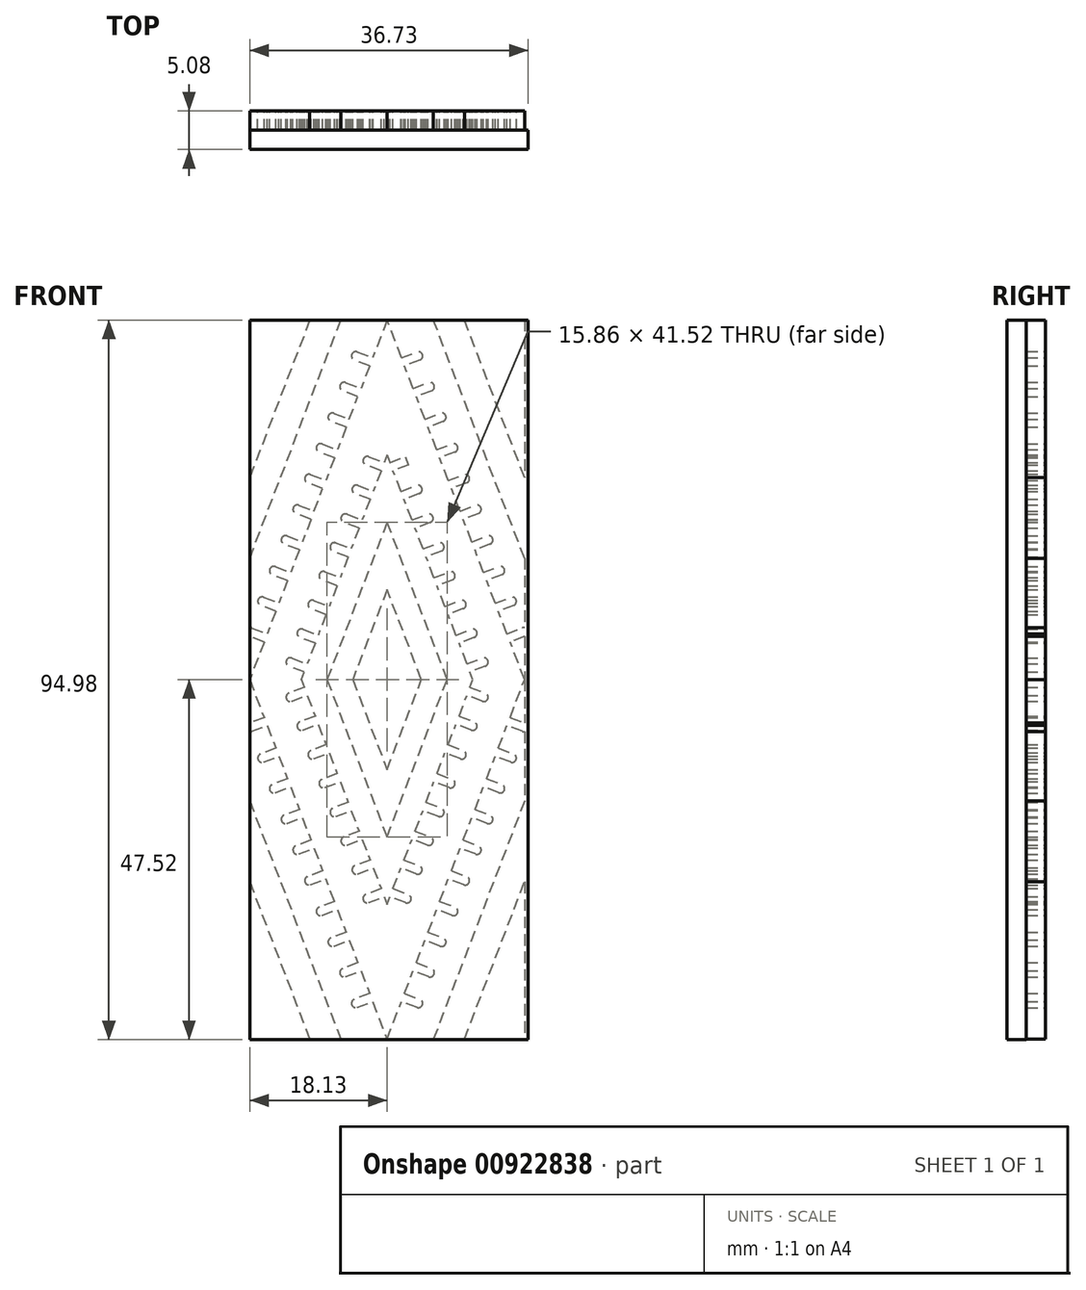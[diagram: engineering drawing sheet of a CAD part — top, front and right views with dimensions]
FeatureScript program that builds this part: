
annotation { "Feature Type Name" : "Feature", "Feature Type Description" : "" }
export const myFeature = defineFeature(function(context is Context, id is Id, definition is map)
    precondition{}
    {
        {
            var Q0;
            Q0=qCreatedBy(makeId("Front.planeOp"),FACE);
            var sketch = newSketch(context, id + "F0", { "sketchPlane" : qUnion([Q0])});
            skLineSegment(sketch, "E0.bottom", {"start": v(-18.13, 47.46) * mm, "end": v(18.13, 47.46) * mm});
            skLineSegment(sketch, "E0.top", {"start": v(-18.13, -47.46) * mm, "end": v(18.13, -47.46) * mm});
            skLineSegment(sketch, "E0.left", {"start": v(-18.13, 47.46) * mm, "end": v(-18.13, -47.46) * mm});
            skLineSegment(sketch, "E0.right", {"start": v(18.13, 47.46) * mm, "end": v(18.13, -47.46) * mm});
            skPoint(sketch, "E0.middle", {"position": v(0, 0) * mm});
            skLineSegment(sketch, "E1", {"start": v(0, 47.46) * mm, "end": v(-1.9, 42.47) * mm});
            skLineSegment(sketch, "E2", {"start": v(-18.13, 0) * mm, "end": v(-16.22, -4.98) * mm});
            skLineSegment(sketch, "E3", {"start": v(0, -47.46) * mm, "end": v(1.9, -42.47) * mm});
            skLineSegment(sketch, "E4", {"start": v(18.13, 0) * mm, "end": v(16.22, 4.98) * mm});
            skLineSegment(sketch, "E5.0", {"start": v(-3.4, 47.46) * mm, "end": v(-18.13, 8.9) * mm});
            skLineSegment(sketch, "E5.1", {"start": v(18.13, 8.9) * mm, "end": v(3.4, 47.46) * mm});
            skLineSegment(sketch, "E5.2", {"start": v(3.4, -47.46) * mm, "end": v(18.13, -8.9) * mm});
            skLineSegment(sketch, "E5.3", {"start": v(-18.13, -8.9) * mm, "end": v(-3.4, -47.46) * mm});
            skLineSegment(sketch, "E6.0", {"start": v(-10.2, 47.46) * mm, "end": v(-18.13, 26.7) * mm});
            skLineSegment(sketch, "E7.0", {"start": v(18.13, 26.7) * mm, "end": v(10.2, 47.46) * mm});
            skLineSegment(sketch, "E8.0", {"start": v(0, 29.66) * mm, "end": v(-0.39, 28.65) * mm});
            skLineSegment(sketch, "E8.1", {"start": v(11.33, 0) * mm, "end": v(10.94, 1) * mm});
            skLineSegment(sketch, "E8.2", {"start": v(0, -29.66) * mm, "end": v(0.39, -28.65) * mm});
            skLineSegment(sketch, "E8.3", {"start": v(-11.33, 0) * mm, "end": v(-10.94, -1) * mm});
            skLineSegment(sketch, "E9.0", {"start": v(4.53, 0) * mm, "end": v(0, 11.86) * mm});
            skLineSegment(sketch, "E9.1", {"start": v(0, -11.86) * mm, "end": v(4.53, 0) * mm});
            skLineSegment(sketch, "E9.2", {"start": v(-4.53, 0) * mm, "end": v(0, -11.86) * mm});
            skLineSegment(sketch, "E9.3", {"start": v(0, 11.86) * mm, "end": v(-4.53, 0) * mm});
            skLineSegment(sketch, "E10.0", {"start": v(0, 20.76) * mm, "end": v(-7.93, 0) * mm});
            skLineSegment(sketch, "E10.1", {"start": v(7.93, 0) * mm, "end": v(0, 20.76) * mm});
            skLineSegment(sketch, "E10.2", {"start": v(0, -20.76) * mm, "end": v(7.93, 0) * mm});
            skLineSegment(sketch, "E10.3", {"start": v(-7.93, 0) * mm, "end": v(0, -20.76) * mm});
            skLineSegment(sketch, "E11", {"start": v(-10.94, 1) * mm, "end": v(-12.96, 1.78) * mm});
            skLineSegment(sketch, "E12", {"start": v(-12.96, 1.78) * mm, "end": v(-12.55, 2.85) * mm});
            skLineSegment(sketch, "E13", {"start": v(-12.55, 2.85) * mm, "end": v(-10.54, 2.08) * mm});
            skArc(sketch, "E14", {"start": v(-12.55, 2.85) * mm, "mid": v(-13.3, 2.52) * mm, "end": v(-12.96, 1.78) * mm});
            skLineSegment(sketch, "E15.1.0.0", {"start": v(-9.5, 4.8) * mm, "end": v(-11.51, 5.58) * mm});
            skLineSegment(sketch, "E15.1.0.1", {"start": v(-11.1, 6.64) * mm, "end": v(-9.09, 5.87) * mm});
            skArc(sketch, "E15.1.0.2", {"start": v(-11.1, 6.64) * mm, "mid": v(-11.84, 6.31) * mm, "end": v(-11.51, 5.58) * mm});
            skLineSegment(sketch, "E15.2.0.0", {"start": v(-8.04, 8.6) * mm, "end": v(-10.06, 9.37) * mm});
            skLineSegment(sketch, "E15.2.0.1", {"start": v(-9.65, 10.44) * mm, "end": v(-7.64, 9.67) * mm});
            skArc(sketch, "E15.2.0.2", {"start": v(-9.65, 10.44) * mm, "mid": v(-10.4, 10.1) * mm, "end": v(-10.06, 9.37) * mm});
            skLineSegment(sketch, "E15.direction1", {"start": v(-12.96, 1.78) * mm, "end": v(-11.51, 5.58) * mm, "construction": true});
            skLineSegment(sketch, "E16.0.3.0", {"start": v(-6.6, 12.4) * mm, "end": v(-8.61, 13.17) * mm});
            skLineSegment(sketch, "E16.3.3.0", {"start": v(-8.2, 14.24) * mm, "end": v(-6.19, 13.47) * mm});
            skArc(sketch, "E16.6.3.0", {"start": v(-8.2, 14.24) * mm, "mid": v(-8.94, 13.9) * mm, "end": v(-8.61, 13.17) * mm});
            skLineSegment(sketch, "E16.0.4.0", {"start": v(-5.14, 16.2) * mm, "end": v(-7.16, 16.96) * mm});
            skLineSegment(sketch, "E16.3.4.0", {"start": v(-6.75, 18.03) * mm, "end": v(-4.74, 17.26) * mm});
            skArc(sketch, "E16.6.4.0", {"start": v(-6.75, 18.03) * mm, "mid": v(-7.5, 17.7) * mm, "end": v(-7.16, 16.96) * mm});
            skLineSegment(sketch, "E16.0.5.0", {"start": v(-3.7, 20) * mm, "end": v(-5.71, 20.76) * mm});
            skLineSegment(sketch, "E16.3.5.0", {"start": v(-5.3, 21.83) * mm, "end": v(-3.29, 21.06) * mm});
            skArc(sketch, "E16.6.5.0", {"start": v(-5.3, 21.83) * mm, "mid": v(-6.04, 21.5) * mm, "end": v(-5.71, 20.76) * mm});
            skLineSegment(sketch, "E16.0.6.0", {"start": v(-2.24, 23.79) * mm, "end": v(-4.26, 24.56) * mm});
            skLineSegment(sketch, "E16.3.6.0", {"start": v(-3.85, 25.63) * mm, "end": v(-1.84, 24.86) * mm});
            skArc(sketch, "E16.6.6.0", {"start": v(-3.85, 25.63) * mm, "mid": v(-4.59, 25.3) * mm, "end": v(-4.26, 24.56) * mm});
            skLineSegment(sketch, "E17", {"start": v(-11.33, 0) * mm, "end": v(-10.94, 1) * mm});
            skLineSegment(sketch, "E18.0.7.0", {"start": v(-0.8, 27.58) * mm, "end": v(-2.8, 28.35) * mm});
            skLineSegment(sketch, "E18.3.7.0", {"start": v(-2.4, 29.42) * mm, "end": v(-0.39, 28.65) * mm});
            skArc(sketch, "E18.6.7.0", {"start": v(-2.4, 29.42) * mm, "mid": v(-3.14, 29.1) * mm, "end": v(-2.8, 28.35) * mm});
            skLineSegment(sketch, "E19", {"start": v(-10.94, -1) * mm, "end": v(-12.96, -1.78) * mm});
            skLineSegment(sketch, "E20", {"start": v(-12.96, -1.78) * mm, "end": v(-12.55, -2.85) * mm});
            skLineSegment(sketch, "E21", {"start": v(-12.55, -2.85) * mm, "end": v(-10.54, -2.08) * mm});
            skArc(sketch, "E22", {"start": v(-12.96, -1.78) * mm, "mid": v(-13.3, -2.52) * mm, "end": v(-12.55, -2.85) * mm});
            skLineSegment(sketch, "E23.1.0.0", {"start": v(-11.1, -6.64) * mm, "end": v(-9.09, -5.87) * mm});
            skLineSegment(sketch, "E23.1.0.1", {"start": v(-9.5, -4.8) * mm, "end": v(-11.51, -5.58) * mm});
            skArc(sketch, "E23.1.0.2", {"start": v(-11.51, -5.58) * mm, "mid": v(-11.84, -6.31) * mm, "end": v(-11.1, -6.64) * mm});
            skLineSegment(sketch, "E23.2.0.0", {"start": v(-9.65, -10.44) * mm, "end": v(-7.64, -9.67) * mm});
            skLineSegment(sketch, "E23.2.0.1", {"start": v(-8.04, -8.6) * mm, "end": v(-10.06, -9.37) * mm});
            skArc(sketch, "E23.2.0.2", {"start": v(-10.06, -9.37) * mm, "mid": v(-10.4, -10.1) * mm, "end": v(-9.65, -10.44) * mm});
            skLineSegment(sketch, "E23.direction1", {"start": v(-12.55, -2.85) * mm, "end": v(-11.1, -6.64) * mm, "construction": true});
            skLineSegment(sketch, "E24.0.3.0", {"start": v(-8.2, -14.24) * mm, "end": v(-6.19, -13.47) * mm});
            skLineSegment(sketch, "E24.3.3.0", {"start": v(-6.6, -12.4) * mm, "end": v(-8.61, -13.17) * mm});
            skArc(sketch, "E24.6.3.0", {"start": v(-8.61, -13.17) * mm, "mid": v(-8.94, -13.9) * mm, "end": v(-8.2, -14.24) * mm});
            skLineSegment(sketch, "E24.0.4.0", {"start": v(-6.75, -18.03) * mm, "end": v(-4.74, -17.26) * mm});
            skLineSegment(sketch, "E24.3.4.0", {"start": v(-5.14, -16.2) * mm, "end": v(-7.16, -16.96) * mm});
            skArc(sketch, "E24.6.4.0", {"start": v(-7.16, -16.96) * mm, "mid": v(-7.5, -17.7) * mm, "end": v(-6.75, -18.03) * mm});
            skLineSegment(sketch, "E24.0.5.0", {"start": v(-5.3, -21.83) * mm, "end": v(-3.29, -21.06) * mm});
            skLineSegment(sketch, "E24.3.5.0", {"start": v(-3.7, -20) * mm, "end": v(-5.71, -20.76) * mm});
            skArc(sketch, "E24.6.5.0", {"start": v(-5.71, -20.76) * mm, "mid": v(-6.04, -21.5) * mm, "end": v(-5.3, -21.83) * mm});
            skLineSegment(sketch, "E24.0.6.0", {"start": v(-3.85, -25.63) * mm, "end": v(-1.84, -24.86) * mm});
            skLineSegment(sketch, "E24.3.6.0", {"start": v(-2.24, -23.79) * mm, "end": v(-4.26, -24.56) * mm});
            skArc(sketch, "E24.6.6.0", {"start": v(-4.26, -24.56) * mm, "mid": v(-4.59, -25.3) * mm, "end": v(-3.85, -25.63) * mm});
            skLineSegment(sketch, "E24.0.7.0", {"start": v(-2.4, -29.42) * mm, "end": v(-0.39, -28.65) * mm});
            skLineSegment(sketch, "E24.3.7.0", {"start": v(-0.8, -27.58) * mm, "end": v(-2.8, -28.35) * mm});
            skArc(sketch, "E24.6.7.0", {"start": v(-2.8, -28.35) * mm, "mid": v(-3.14, -29.1) * mm, "end": v(-2.4, -29.42) * mm});
            skLineSegment(sketch, "E25", {"start": v(18.13, 47.46) * mm, "end": v(-18.13, -47.46) * mm, "construction": true});
            skLineSegment(sketch, "E26", {"start": v(-18.13, 47.46) * mm, "end": v(18.13, -47.46) * mm, "construction": true});
            skLineSegment(sketch, "E27", {"start": v(0, 47.46) * mm, "end": v(0, -47.46) * mm, "construction": true});
            skLineSegment(sketch, "E28", {"start": v(-18.13, 0) * mm, "end": v(18.13, 0) * mm, "construction": true});
            skLineSegment(sketch, "E29", {"start": v(0, 29.66) * mm, "end": v(0.39, 28.65) * mm});
            skLineSegment(sketch, "E30", {"start": v(0.39, 28.65) * mm, "end": v(2.4, 29.42) * mm});
            skLineSegment(sketch, "E31", {"start": v(2.4, 29.42) * mm, "end": v(2.8, 28.35) * mm});
            skLineSegment(sketch, "E32", {"start": v(2.8, 28.35) * mm, "end": v(0.8, 27.58) * mm});
            skArc(sketch, "E33", {"start": v(2.8, 28.35) * mm, "mid": v(3.14, 29.1) * mm, "end": v(2.4, 29.42) * mm});
            skLineSegment(sketch, "E34.1.0.0", {"start": v(1.84, 24.86) * mm, "end": v(3.85, 25.63) * mm});
            skArc(sketch, "E34.1.0.1", {"start": v(4.26, 24.56) * mm, "mid": v(4.59, 25.3) * mm, "end": v(3.85, 25.63) * mm});
            skLineSegment(sketch, "E34.1.0.2", {"start": v(4.26, 24.56) * mm, "end": v(2.24, 23.79) * mm});
            skLineSegment(sketch, "E34.2.0.0", {"start": v(3.29, 21.06) * mm, "end": v(5.3, 21.83) * mm});
            skArc(sketch, "E34.2.0.1", {"start": v(5.71, 20.76) * mm, "mid": v(6.04, 21.5) * mm, "end": v(5.3, 21.83) * mm});
            skLineSegment(sketch, "E34.2.0.2", {"start": v(5.71, 20.76) * mm, "end": v(3.7, 20) * mm});
            skLineSegment(sketch, "E34.direction1", {"start": v(0.8, 27.58) * mm, "end": v(1.84, 24.86) * mm, "construction": true});
            skLineSegment(sketch, "E35.0.3.0", {"start": v(4.74, 17.26) * mm, "end": v(6.75, 18.03) * mm});
            skArc(sketch, "E35.3.3.0", {"start": v(7.16, 16.96) * mm, "mid": v(7.5, 17.7) * mm, "end": v(6.75, 18.03) * mm});
            skLineSegment(sketch, "E35.7.3.0", {"start": v(7.16, 16.96) * mm, "end": v(5.14, 16.2) * mm});
            skLineSegment(sketch, "E35.0.4.0", {"start": v(6.19, 13.47) * mm, "end": v(8.2, 14.24) * mm});
            skArc(sketch, "E35.3.4.0", {"start": v(8.61, 13.17) * mm, "mid": v(8.94, 13.9) * mm, "end": v(8.2, 14.24) * mm});
            skLineSegment(sketch, "E35.7.4.0", {"start": v(8.61, 13.17) * mm, "end": v(6.6, 12.4) * mm});
            skLineSegment(sketch, "E35.0.5.0", {"start": v(7.64, 9.67) * mm, "end": v(9.65, 10.44) * mm});
            skArc(sketch, "E35.3.5.0", {"start": v(10.06, 9.37) * mm, "mid": v(10.4, 10.1) * mm, "end": v(9.65, 10.44) * mm});
            skLineSegment(sketch, "E35.7.5.0", {"start": v(10.06, 9.37) * mm, "end": v(8.04, 8.6) * mm});
            skLineSegment(sketch, "E35.0.6.0", {"start": v(9.09, 5.87) * mm, "end": v(11.1, 6.64) * mm});
            skArc(sketch, "E35.3.6.0", {"start": v(11.51, 5.58) * mm, "mid": v(11.84, 6.31) * mm, "end": v(11.1, 6.64) * mm});
            skLineSegment(sketch, "E35.7.6.0", {"start": v(11.51, 5.58) * mm, "end": v(9.5, 4.8) * mm});
            skLineSegment(sketch, "E35.0.7.0", {"start": v(10.54, 2.08) * mm, "end": v(12.55, 2.85) * mm});
            skArc(sketch, "E35.3.7.0", {"start": v(12.96, 1.78) * mm, "mid": v(13.3, 2.52) * mm, "end": v(12.55, 2.85) * mm});
            skLineSegment(sketch, "E35.7.7.0", {"start": v(12.96, 1.78) * mm, "end": v(10.94, 1) * mm});
            skLineSegment(sketch, "E36", {"start": v(10.94, -1) * mm, "end": v(12.96, -1.78) * mm});
            skLineSegment(sketch, "E37", {"start": v(12.96, -1.78) * mm, "end": v(12.55, -2.85) * mm});
            skLineSegment(sketch, "E38", {"start": v(12.55, -2.85) * mm, "end": v(10.54, -2.08) * mm});
            skArc(sketch, "E39", {"start": v(12.55, -2.85) * mm, "mid": v(13.3, -2.52) * mm, "end": v(12.96, -1.78) * mm});
            skLineSegment(sketch, "E40", {"start": v(-16.22, 4.98) * mm, "end": v(-18.24, 5.75) * mm});
            skLineSegment(sketch, "E41", {"start": v(-18.24, 5.75) * mm, "end": v(-17.83, 6.82) * mm});
            skLineSegment(sketch, "E42", {"start": v(-17.83, 6.82) * mm, "end": v(-15.82, 6.05) * mm});
            skArc(sketch, "E43", {"start": v(-17.83, 6.82) * mm, "mid": v(-18.57, 6.5) * mm, "end": v(-18.24, 5.75) * mm});
            skLineSegment(sketch, "E44.1.0.0", {"start": v(11.1, -6.64) * mm, "end": v(9.09, -5.87) * mm});
            skLineSegment(sketch, "E44.1.0.1", {"start": v(9.5, -4.8) * mm, "end": v(11.51, -5.58) * mm});
            skArc(sketch, "E44.1.0.2", {"start": v(11.1, -6.64) * mm, "mid": v(11.84, -6.31) * mm, "end": v(11.51, -5.58) * mm});
            skLineSegment(sketch, "E44.2.0.0", {"start": v(9.65, -10.44) * mm, "end": v(7.64, -9.67) * mm});
            skLineSegment(sketch, "E44.2.0.1", {"start": v(8.04, -8.6) * mm, "end": v(10.06, -9.37) * mm});
            skArc(sketch, "E44.2.0.2", {"start": v(9.65, -10.44) * mm, "mid": v(10.4, -10.1) * mm, "end": v(10.06, -9.37) * mm});
            skLineSegment(sketch, "E44.3.0.0", {"start": v(8.2, -14.24) * mm, "end": v(6.19, -13.47) * mm});
            skLineSegment(sketch, "E44.3.0.1", {"start": v(6.6, -12.4) * mm, "end": v(8.61, -13.17) * mm});
            skArc(sketch, "E44.3.0.2", {"start": v(8.2, -14.24) * mm, "mid": v(8.94, -13.9) * mm, "end": v(8.61, -13.17) * mm});
            skLineSegment(sketch, "E44.4.0.0", {"start": v(6.75, -18.03) * mm, "end": v(4.74, -17.26) * mm});
            skLineSegment(sketch, "E44.4.0.1", {"start": v(5.14, -16.2) * mm, "end": v(7.16, -16.96) * mm});
            skArc(sketch, "E44.4.0.2", {"start": v(6.75, -18.03) * mm, "mid": v(7.5, -17.7) * mm, "end": v(7.16, -16.96) * mm});
            skLineSegment(sketch, "E44.5.0.0", {"start": v(5.3, -21.83) * mm, "end": v(3.29, -21.06) * mm});
            skLineSegment(sketch, "E44.5.0.1", {"start": v(3.7, -20) * mm, "end": v(5.71, -20.76) * mm});
            skArc(sketch, "E44.5.0.2", {"start": v(5.3, -21.83) * mm, "mid": v(6.04, -21.5) * mm, "end": v(5.71, -20.76) * mm});
            skLineSegment(sketch, "E44.6.0.0", {"start": v(3.85, -25.63) * mm, "end": v(1.84, -24.86) * mm});
            skLineSegment(sketch, "E44.6.0.1", {"start": v(2.24, -23.79) * mm, "end": v(4.26, -24.56) * mm});
            skArc(sketch, "E44.6.0.2", {"start": v(3.85, -25.63) * mm, "mid": v(4.59, -25.3) * mm, "end": v(4.26, -24.56) * mm});
            skLineSegment(sketch, "E44.7.0.0", {"start": v(2.4, -29.42) * mm, "end": v(0.39, -28.65) * mm});
            skLineSegment(sketch, "E44.7.0.1", {"start": v(0.8, -27.58) * mm, "end": v(2.8, -28.35) * mm});
            skArc(sketch, "E44.7.0.2", {"start": v(2.4, -29.42) * mm, "mid": v(3.14, -29.1) * mm, "end": v(2.8, -28.35) * mm});
            skLineSegment(sketch, "E44.direction1", {"start": v(10.54, -2.08) * mm, "end": v(9.5, -4.8) * mm, "construction": true});
            skLineSegment(sketch, "E45.1.0.0", {"start": v(-14.68, 9.03) * mm, "end": v(-16.7, 9.8) * mm});
            skLineSegment(sketch, "E45.1.0.1", {"start": v(-16.29, 10.87) * mm, "end": v(-14.27, 10.1) * mm});
            skArc(sketch, "E45.1.0.2", {"start": v(-16.29, 10.87) * mm, "mid": v(-17.02, 10.54) * mm, "end": v(-16.7, 9.8) * mm});
            skLineSegment(sketch, "E45.2.0.0", {"start": v(-13.13, 13.08) * mm, "end": v(-15.15, 13.85) * mm});
            skLineSegment(sketch, "E45.2.0.1", {"start": v(-14.74, 14.91) * mm, "end": v(-12.72, 14.14) * mm});
            skArc(sketch, "E45.2.0.2", {"start": v(-14.74, 14.91) * mm, "mid": v(-15.48, 14.58) * mm, "end": v(-15.15, 13.85) * mm});
            skLineSegment(sketch, "E45.3.0.0", {"start": v(-11.59, 17.12) * mm, "end": v(-13.6, 17.9) * mm});
            skLineSegment(sketch, "E45.3.0.1", {"start": v(-13.2, 18.96) * mm, "end": v(-11.18, 18.2) * mm});
            skArc(sketch, "E45.3.0.2", {"start": v(-13.2, 18.96) * mm, "mid": v(-13.93, 18.63) * mm, "end": v(-13.6, 17.9) * mm});
            skLineSegment(sketch, "E45.4.0.0", {"start": v(-10.04, 21.17) * mm, "end": v(-12.06, 21.94) * mm});
            skLineSegment(sketch, "E45.4.0.1", {"start": v(-11.65, 23) * mm, "end": v(-9.63, 22.24) * mm});
            skArc(sketch, "E45.4.0.2", {"start": v(-11.65, 23) * mm, "mid": v(-12.39, 22.68) * mm, "end": v(-12.06, 21.94) * mm});
            skLineSegment(sketch, "E45.5.0.0", {"start": v(-8.5, 25.22) * mm, "end": v(-10.51, 25.99) * mm});
            skLineSegment(sketch, "E45.5.0.1", {"start": v(-10.1, 27.06) * mm, "end": v(-8.09, 26.29) * mm});
            skArc(sketch, "E45.5.0.2", {"start": v(-10.1, 27.06) * mm, "mid": v(-10.84, 26.73) * mm, "end": v(-10.51, 25.99) * mm});
            skLineSegment(sketch, "E45.6.0.0", {"start": v(-6.95, 29.26) * mm, "end": v(-8.97, 30.03) * mm});
            skLineSegment(sketch, "E45.6.0.1", {"start": v(-8.56, 31.1) * mm, "end": v(-6.54, 30.33) * mm});
            skArc(sketch, "E45.6.0.2", {"start": v(-8.56, 31.1) * mm, "mid": v(-9.3, 30.77) * mm, "end": v(-8.97, 30.03) * mm});
            skLineSegment(sketch, "E45.7.0.0", {"start": v(-5.4, 33.31) * mm, "end": v(-7.42, 34.08) * mm});
            skLineSegment(sketch, "E45.7.0.1", {"start": v(-7.01, 35.15) * mm, "end": v(-5, 34.38) * mm});
            skArc(sketch, "E45.7.0.2", {"start": v(-7.01, 35.15) * mm, "mid": v(-7.75, 34.82) * mm, "end": v(-7.42, 34.08) * mm});
            skLineSegment(sketch, "E45.8.0.0", {"start": v(-3.86, 37.36) * mm, "end": v(-5.87, 38.13) * mm});
            skLineSegment(sketch, "E45.8.0.1", {"start": v(-5.47, 39.2) * mm, "end": v(-3.45, 38.43) * mm});
            skArc(sketch, "E45.8.0.2", {"start": v(-5.47, 39.2) * mm, "mid": v(-6.2, 38.87) * mm, "end": v(-5.87, 38.13) * mm});
            skLineSegment(sketch, "E45.9.0.0", {"start": v(-2.31, 41.4) * mm, "end": v(-4.33, 42.18) * mm});
            skLineSegment(sketch, "E45.9.0.1", {"start": v(-3.92, 43.24) * mm, "end": v(-1.9, 42.47) * mm});
            skArc(sketch, "E45.9.0.2", {"start": v(-3.92, 43.24) * mm, "mid": v(-4.66, 42.91) * mm, "end": v(-4.33, 42.18) * mm});
            skLineSegment(sketch, "E45.direction1", {"start": v(-18.24, 5.75) * mm, "end": v(-16.7, 9.8) * mm, "construction": true});
            skLineSegment(sketch, "E46", {"start": v(1.9, 42.47) * mm, "end": v(3.92, 43.24) * mm});
            skLineSegment(sketch, "E47", {"start": v(3.92, 43.24) * mm, "end": v(4.12, 42.7) * mm});
            skLineSegment(sketch, "E48", {"start": v(4.33, 42.18) * mm, "end": v(2.31, 41.4) * mm});
            skArc(sketch, "E49", {"start": v(4.33, 42.18) * mm, "mid": v(4.66, 42.91) * mm, "end": v(3.92, 43.24) * mm});
            skLineSegment(sketch, "E50.1.0.0", {"start": v(5.87, 38.13) * mm, "end": v(3.86, 37.36) * mm});
            skLineSegment(sketch, "E50.1.0.1", {"start": v(3.45, 38.43) * mm, "end": v(5.47, 39.2) * mm});
            skArc(sketch, "E50.1.0.2", {"start": v(5.87, 38.13) * mm, "mid": v(6.2, 38.87) * mm, "end": v(5.47, 39.2) * mm});
            skLineSegment(sketch, "E50.2.0.0", {"start": v(7.42, 34.08) * mm, "end": v(5.4, 33.31) * mm});
            skLineSegment(sketch, "E50.2.0.1", {"start": v(5, 34.38) * mm, "end": v(7.01, 35.15) * mm});
            skArc(sketch, "E50.2.0.2", {"start": v(7.42, 34.08) * mm, "mid": v(7.75, 34.82) * mm, "end": v(7.01, 35.15) * mm});
            skLineSegment(sketch, "E50.3.0.0", {"start": v(8.97, 30.03) * mm, "end": v(6.95, 29.26) * mm});
            skLineSegment(sketch, "E50.3.0.1", {"start": v(6.54, 30.33) * mm, "end": v(8.56, 31.1) * mm});
            skArc(sketch, "E50.3.0.2", {"start": v(8.97, 30.03) * mm, "mid": v(9.3, 30.77) * mm, "end": v(8.56, 31.1) * mm});
            skLineSegment(sketch, "E50.4.0.0", {"start": v(10.51, 25.99) * mm, "end": v(8.5, 25.22) * mm});
            skLineSegment(sketch, "E50.4.0.1", {"start": v(8.09, 26.29) * mm, "end": v(10.1, 27.06) * mm});
            skArc(sketch, "E50.4.0.2", {"start": v(10.51, 25.99) * mm, "mid": v(10.84, 26.73) * mm, "end": v(10.1, 27.06) * mm});
            skLineSegment(sketch, "E50.5.0.0", {"start": v(12.06, 21.94) * mm, "end": v(10.04, 21.17) * mm});
            skLineSegment(sketch, "E50.5.0.1", {"start": v(9.63, 22.24) * mm, "end": v(11.65, 23) * mm});
            skArc(sketch, "E50.5.0.2", {"start": v(12.06, 21.94) * mm, "mid": v(12.39, 22.68) * mm, "end": v(11.65, 23) * mm});
            skLineSegment(sketch, "E50.6.0.0", {"start": v(13.6, 17.9) * mm, "end": v(11.59, 17.12) * mm});
            skLineSegment(sketch, "E50.6.0.1", {"start": v(11.18, 18.2) * mm, "end": v(13.2, 18.96) * mm});
            skArc(sketch, "E50.6.0.2", {"start": v(13.6, 17.9) * mm, "mid": v(13.93, 18.63) * mm, "end": v(13.2, 18.96) * mm});
            skLineSegment(sketch, "E50.7.0.0", {"start": v(15.15, 13.85) * mm, "end": v(13.13, 13.08) * mm});
            skLineSegment(sketch, "E50.7.0.1", {"start": v(12.72, 14.14) * mm, "end": v(14.74, 14.91) * mm});
            skArc(sketch, "E50.7.0.2", {"start": v(15.15, 13.85) * mm, "mid": v(15.48, 14.58) * mm, "end": v(14.74, 14.91) * mm});
            skLineSegment(sketch, "E50.8.0.0", {"start": v(16.7, 9.8) * mm, "end": v(14.68, 9.03) * mm});
            skLineSegment(sketch, "E50.8.0.1", {"start": v(14.27, 10.1) * mm, "end": v(16.29, 10.87) * mm});
            skArc(sketch, "E50.8.0.2", {"start": v(16.7, 9.8) * mm, "mid": v(17.02, 10.54) * mm, "end": v(16.29, 10.87) * mm});
            skLineSegment(sketch, "E50.9.0.0", {"start": v(18.24, 5.75) * mm, "end": v(16.22, 4.98) * mm});
            skLineSegment(sketch, "E50.9.0.1", {"start": v(15.82, 6.05) * mm, "end": v(17.83, 6.82) * mm});
            skArc(sketch, "E50.9.0.2", {"start": v(18.24, 5.75) * mm, "mid": v(18.57, 6.5) * mm, "end": v(17.83, 6.82) * mm});
            skLineSegment(sketch, "E50.direction1", {"start": v(2.31, 41.4) * mm, "end": v(3.45, 38.43) * mm, "construction": true});
            skLineSegment(sketch, "E51", {"start": v(-16.22, -4.98) * mm, "end": v(-18.24, -5.75) * mm});
            skLineSegment(sketch, "E52", {"start": v(-18.24, -5.75) * mm, "end": v(-17.83, -6.82) * mm});
            skLineSegment(sketch, "E53", {"start": v(-17.83, -6.82) * mm, "end": v(-15.82, -6.05) * mm});
            skArc(sketch, "E54", {"start": v(-18.24, -5.75) * mm, "mid": v(-18.57, -6.5) * mm, "end": v(-17.83, -6.82) * mm});
            skLineSegment(sketch, "E55.1.0.0", {"start": v(-14.68, -9.03) * mm, "end": v(-16.7, -9.8) * mm});
            skLineSegment(sketch, "E55.1.0.1", {"start": v(-16.29, -10.87) * mm, "end": v(-14.27, -10.1) * mm});
            skArc(sketch, "E55.1.0.2", {"start": v(-16.7, -9.8) * mm, "mid": v(-17.02, -10.54) * mm, "end": v(-16.29, -10.87) * mm});
            skLineSegment(sketch, "E55.2.0.0", {"start": v(-13.13, -13.08) * mm, "end": v(-15.15, -13.85) * mm});
            skLineSegment(sketch, "E55.2.0.1", {"start": v(-14.74, -14.91) * mm, "end": v(-12.72, -14.14) * mm});
            skArc(sketch, "E55.2.0.2", {"start": v(-15.15, -13.85) * mm, "mid": v(-15.48, -14.58) * mm, "end": v(-14.74, -14.91) * mm});
            skLineSegment(sketch, "E55.3.0.0", {"start": v(-11.59, -17.12) * mm, "end": v(-13.6, -17.9) * mm});
            skLineSegment(sketch, "E55.3.0.1", {"start": v(-13.2, -18.96) * mm, "end": v(-11.18, -18.2) * mm});
            skArc(sketch, "E55.3.0.2", {"start": v(-13.6, -17.9) * mm, "mid": v(-13.93, -18.63) * mm, "end": v(-13.2, -18.96) * mm});
            skLineSegment(sketch, "E55.4.0.0", {"start": v(-10.04, -21.17) * mm, "end": v(-12.06, -21.94) * mm});
            skLineSegment(sketch, "E55.4.0.1", {"start": v(-11.65, -23) * mm, "end": v(-9.63, -22.24) * mm});
            skArc(sketch, "E55.4.0.2", {"start": v(-12.06, -21.94) * mm, "mid": v(-12.39, -22.68) * mm, "end": v(-11.65, -23) * mm});
            skLineSegment(sketch, "E55.5.0.0", {"start": v(-8.5, -25.22) * mm, "end": v(-10.51, -25.99) * mm});
            skLineSegment(sketch, "E55.5.0.1", {"start": v(-10.1, -27.06) * mm, "end": v(-8.09, -26.29) * mm});
            skArc(sketch, "E55.5.0.2", {"start": v(-10.51, -25.99) * mm, "mid": v(-10.84, -26.73) * mm, "end": v(-10.1, -27.06) * mm});
            skLineSegment(sketch, "E55.6.0.0", {"start": v(-6.95, -29.26) * mm, "end": v(-8.97, -30.03) * mm});
            skLineSegment(sketch, "E55.6.0.1", {"start": v(-8.56, -31.1) * mm, "end": v(-6.54, -30.33) * mm});
            skArc(sketch, "E55.6.0.2", {"start": v(-8.97, -30.03) * mm, "mid": v(-9.3, -30.77) * mm, "end": v(-8.56, -31.1) * mm});
            skLineSegment(sketch, "E55.7.0.0", {"start": v(-5.4, -33.31) * mm, "end": v(-7.42, -34.08) * mm});
            skLineSegment(sketch, "E55.7.0.1", {"start": v(-7.01, -35.15) * mm, "end": v(-5, -34.38) * mm});
            skArc(sketch, "E55.7.0.2", {"start": v(-7.42, -34.08) * mm, "mid": v(-7.75, -34.82) * mm, "end": v(-7.01, -35.15) * mm});
            skLineSegment(sketch, "E55.8.0.0", {"start": v(-3.86, -37.36) * mm, "end": v(-5.87, -38.13) * mm});
            skLineSegment(sketch, "E55.8.0.1", {"start": v(-5.47, -39.2) * mm, "end": v(-3.45, -38.43) * mm});
            skArc(sketch, "E55.8.0.2", {"start": v(-5.87, -38.13) * mm, "mid": v(-6.2, -38.87) * mm, "end": v(-5.47, -39.2) * mm});
            skLineSegment(sketch, "E55.9.0.0", {"start": v(-2.31, -41.4) * mm, "end": v(-4.33, -42.18) * mm});
            skLineSegment(sketch, "E55.9.0.1", {"start": v(-3.92, -43.24) * mm, "end": v(-1.9, -42.47) * mm});
            skArc(sketch, "E55.9.0.2", {"start": v(-4.33, -42.18) * mm, "mid": v(-4.66, -42.91) * mm, "end": v(-3.92, -43.24) * mm});
            skLineSegment(sketch, "E55.direction1", {"start": v(-18.24, -5.75) * mm, "end": v(-16.7, -9.8) * mm, "construction": true});
            skLineSegment(sketch, "E56", {"start": v(16.22, -4.98) * mm, "end": v(18.24, -5.75) * mm});
            skLineSegment(sketch, "E57", {"start": v(18.24, -5.75) * mm, "end": v(17.83, -6.82) * mm});
            skLineSegment(sketch, "E58", {"start": v(17.83, -6.82) * mm, "end": v(15.82, -6.05) * mm});
            skArc(sketch, "E59", {"start": v(17.83, -6.82) * mm, "mid": v(18.57, -6.5) * mm, "end": v(18.24, -5.75) * mm});
            skLineSegment(sketch, "E60.1.0.0", {"start": v(14.68, -9.03) * mm, "end": v(16.7, -9.8) * mm});
            skLineSegment(sketch, "E60.1.0.1", {"start": v(16.29, -10.87) * mm, "end": v(14.27, -10.1) * mm});
            skArc(sketch, "E60.1.0.2", {"start": v(16.29, -10.87) * mm, "mid": v(17.02, -10.54) * mm, "end": v(16.7, -9.8) * mm});
            skLineSegment(sketch, "E60.2.0.0", {"start": v(13.13, -13.08) * mm, "end": v(15.15, -13.85) * mm});
            skLineSegment(sketch, "E60.2.0.1", {"start": v(14.74, -14.91) * mm, "end": v(12.72, -14.14) * mm});
            skArc(sketch, "E60.2.0.2", {"start": v(14.74, -14.91) * mm, "mid": v(15.48, -14.58) * mm, "end": v(15.15, -13.85) * mm});
            skLineSegment(sketch, "E60.3.0.0", {"start": v(11.59, -17.12) * mm, "end": v(13.6, -17.9) * mm});
            skLineSegment(sketch, "E60.3.0.1", {"start": v(13.2, -18.96) * mm, "end": v(11.18, -18.2) * mm});
            skArc(sketch, "E60.3.0.2", {"start": v(13.2, -18.96) * mm, "mid": v(13.93, -18.63) * mm, "end": v(13.6, -17.9) * mm});
            skLineSegment(sketch, "E60.4.0.0", {"start": v(10.04, -21.17) * mm, "end": v(12.06, -21.94) * mm});
            skLineSegment(sketch, "E60.4.0.1", {"start": v(11.65, -23) * mm, "end": v(9.63, -22.24) * mm});
            skArc(sketch, "E60.4.0.2", {"start": v(11.65, -23) * mm, "mid": v(12.39, -22.68) * mm, "end": v(12.06, -21.94) * mm});
            skLineSegment(sketch, "E60.5.0.0", {"start": v(8.5, -25.22) * mm, "end": v(10.51, -25.99) * mm});
            skLineSegment(sketch, "E60.5.0.1", {"start": v(10.1, -27.06) * mm, "end": v(8.09, -26.29) * mm});
            skArc(sketch, "E60.5.0.2", {"start": v(10.1, -27.06) * mm, "mid": v(10.84, -26.73) * mm, "end": v(10.51, -25.99) * mm});
            skLineSegment(sketch, "E60.6.0.0", {"start": v(6.95, -29.26) * mm, "end": v(8.97, -30.03) * mm});
            skLineSegment(sketch, "E60.6.0.1", {"start": v(8.56, -31.1) * mm, "end": v(6.54, -30.33) * mm});
            skArc(sketch, "E60.6.0.2", {"start": v(8.56, -31.1) * mm, "mid": v(9.3, -30.77) * mm, "end": v(8.97, -30.03) * mm});
            skLineSegment(sketch, "E60.7.0.0", {"start": v(5.4, -33.31) * mm, "end": v(7.42, -34.08) * mm});
            skLineSegment(sketch, "E60.7.0.1", {"start": v(7.01, -35.15) * mm, "end": v(5, -34.38) * mm});
            skArc(sketch, "E60.7.0.2", {"start": v(7.01, -35.15) * mm, "mid": v(7.75, -34.82) * mm, "end": v(7.42, -34.08) * mm});
            skLineSegment(sketch, "E60.8.0.0", {"start": v(3.86, -37.36) * mm, "end": v(5.87, -38.13) * mm});
            skLineSegment(sketch, "E60.8.0.1", {"start": v(5.47, -39.2) * mm, "end": v(3.45, -38.43) * mm});
            skArc(sketch, "E60.8.0.2", {"start": v(5.47, -39.2) * mm, "mid": v(6.2, -38.87) * mm, "end": v(5.87, -38.13) * mm});
            skLineSegment(sketch, "E60.9.0.0", {"start": v(2.31, -41.4) * mm, "end": v(4.33, -42.18) * mm});
            skLineSegment(sketch, "E60.9.0.1", {"start": v(3.92, -43.24) * mm, "end": v(1.9, -42.47) * mm});
            skArc(sketch, "E60.9.0.2", {"start": v(3.92, -43.24) * mm, "mid": v(4.66, -42.91) * mm, "end": v(4.33, -42.18) * mm});
            skLineSegment(sketch, "E60.direction1", {"start": v(15.82, -6.05) * mm, "end": v(14.68, -9.03) * mm, "construction": true});
            skLineSegment(sketch, "E61.0", {"start": v(-18.13, -26.7) * mm, "end": v(-10.2, -47.46) * mm});
            skLineSegment(sketch, "E62.0", {"start": v(10.2, -47.46) * mm, "end": v(18.13, -26.7) * mm});
            skLineSegment(sketch, "E63.trimOffspring", {"start": v(2.31, -41.4) * mm, "end": v(3.45, -38.43) * mm});
            skLineSegment(sketch, "E64.trimOffspring", {"start": v(3.86, -37.36) * mm, "end": v(5, -34.38) * mm});
            skLineSegment(sketch, "E65.trimOffspring", {"start": v(5.4, -33.31) * mm, "end": v(6.54, -30.33) * mm});
            skLineSegment(sketch, "E66.trimOffspring", {"start": v(6.95, -29.26) * mm, "end": v(8.09, -26.29) * mm});
            skLineSegment(sketch, "E67.trimOffspring", {"start": v(8.5, -25.22) * mm, "end": v(9.63, -22.24) * mm});
            skLineSegment(sketch, "E68.trimOffspring", {"start": v(10.04, -21.17) * mm, "end": v(11.18, -18.2) * mm});
            skLineSegment(sketch, "E69.trimOffspring", {"start": v(11.59, -17.12) * mm, "end": v(12.72, -14.14) * mm});
            skLineSegment(sketch, "E70.trimOffspring", {"start": v(13.13, -13.08) * mm, "end": v(14.27, -10.1) * mm});
            skLineSegment(sketch, "E71.trimOffspring", {"start": v(14.68, -9.03) * mm, "end": v(15.82, -6.05) * mm});
            skLineSegment(sketch, "E72.trimOffspring", {"start": v(16.22, -4.98) * mm, "end": v(18.13, 0) * mm});
            skLineSegment(sketch, "E73.trimOffspring", {"start": v(10.94, -1) * mm, "end": v(11.33, 0) * mm});
            skLineSegment(sketch, "E74.trimOffspring", {"start": v(9.5, -4.8) * mm, "end": v(10.54, -2.08) * mm});
            skLineSegment(sketch, "E75.trimOffspring", {"start": v(8.04, -8.6) * mm, "end": v(9.09, -5.87) * mm});
            skLineSegment(sketch, "E76.trimOffspring", {"start": v(6.6, -12.4) * mm, "end": v(7.64, -9.67) * mm});
            skLineSegment(sketch, "E77.trimOffspring", {"start": v(5.14, -16.2) * mm, "end": v(6.19, -13.47) * mm});
            skLineSegment(sketch, "E78.trimOffspring", {"start": v(3.7, -20) * mm, "end": v(4.74, -17.26) * mm});
            skLineSegment(sketch, "E79.trimOffspring", {"start": v(2.24, -23.79) * mm, "end": v(3.29, -21.06) * mm});
            skLineSegment(sketch, "E80.trimOffspring", {"start": v(0.8, -27.58) * mm, "end": v(1.84, -24.86) * mm});
            skLineSegment(sketch, "E81.trimOffspring", {"start": v(-0.39, -28.65) * mm, "end": v(0, -29.66) * mm});
            skLineSegment(sketch, "E82.trimOffspring", {"start": v(-1.84, -24.86) * mm, "end": v(-0.8, -27.58) * mm});
            skLineSegment(sketch, "E83.trimOffspring", {"start": v(-3.29, -21.06) * mm, "end": v(-2.24, -23.79) * mm});
            skLineSegment(sketch, "E84.trimOffspring", {"start": v(-4.74, -17.26) * mm, "end": v(-3.7, -20) * mm});
            skLineSegment(sketch, "E85.trimOffspring", {"start": v(-6.19, -13.47) * mm, "end": v(-5.14, -16.2) * mm});
            skLineSegment(sketch, "E86.trimOffspring", {"start": v(-7.64, -9.67) * mm, "end": v(-6.6, -12.4) * mm});
            skLineSegment(sketch, "E87.trimOffspring", {"start": v(-9.09, -5.87) * mm, "end": v(-8.04, -8.6) * mm});
            skLineSegment(sketch, "E88.trimOffspring", {"start": v(-10.54, -2.08) * mm, "end": v(-9.5, -4.8) * mm});
            skLineSegment(sketch, "E89.trimOffspring", {"start": v(-10.94, 1) * mm, "end": v(-11.33, 0) * mm});
            skLineSegment(sketch, "E90.trimOffspring", {"start": v(-9.5, 4.8) * mm, "end": v(-10.54, 2.08) * mm});
            skLineSegment(sketch, "E91.trimOffspring", {"start": v(-8.04, 8.6) * mm, "end": v(-9.09, 5.87) * mm});
            skLineSegment(sketch, "E92.trimOffspring", {"start": v(-6.6, 12.4) * mm, "end": v(-7.64, 9.67) * mm});
            skLineSegment(sketch, "E93.trimOffspring", {"start": v(-5.14, 16.2) * mm, "end": v(-6.19, 13.47) * mm});
            skLineSegment(sketch, "E94.trimOffspring", {"start": v(-3.7, 20) * mm, "end": v(-4.74, 17.26) * mm});
            skLineSegment(sketch, "E95.trimOffspring", {"start": v(-2.24, 23.79) * mm, "end": v(-3.29, 21.06) * mm});
            skLineSegment(sketch, "E96.trimOffspring", {"start": v(-0.8, 27.58) * mm, "end": v(-1.84, 24.86) * mm});
            skLineSegment(sketch, "E97.trimOffspring", {"start": v(0.39, 28.65) * mm, "end": v(0, 29.66) * mm});
            skLineSegment(sketch, "E98.trimOffspring", {"start": v(1.84, 24.86) * mm, "end": v(0.8, 27.58) * mm});
            skLineSegment(sketch, "E99.trimOffspring", {"start": v(3.29, 21.06) * mm, "end": v(2.24, 23.79) * mm});
            skLineSegment(sketch, "E100.trimOffspring", {"start": v(4.74, 17.26) * mm, "end": v(3.7, 20) * mm});
            skLineSegment(sketch, "E101.trimOffspring", {"start": v(6.19, 13.47) * mm, "end": v(5.14, 16.2) * mm});
            skLineSegment(sketch, "E102.trimOffspring", {"start": v(7.64, 9.67) * mm, "end": v(6.6, 12.4) * mm});
            skLineSegment(sketch, "E103.trimOffspring", {"start": v(9.09, 5.87) * mm, "end": v(8.04, 8.6) * mm});
            skLineSegment(sketch, "E104.trimOffspring", {"start": v(10.54, 2.08) * mm, "end": v(9.5, 4.8) * mm});
            skLineSegment(sketch, "E105.trimOffspring", {"start": v(15.82, 6.05) * mm, "end": v(14.68, 9.03) * mm});
            skLineSegment(sketch, "E106.trimOffspring", {"start": v(14.27, 10.1) * mm, "end": v(13.13, 13.08) * mm});
            skLineSegment(sketch, "E107.trimOffspring", {"start": v(12.72, 14.14) * mm, "end": v(11.59, 17.12) * mm});
            skLineSegment(sketch, "E108.trimOffspring", {"start": v(11.18, 18.2) * mm, "end": v(10.04, 21.17) * mm});
            skLineSegment(sketch, "E109.trimOffspring", {"start": v(9.63, 22.24) * mm, "end": v(8.5, 25.22) * mm});
            skLineSegment(sketch, "E110.trimOffspring", {"start": v(8.09, 26.29) * mm, "end": v(6.95, 29.26) * mm});
            skLineSegment(sketch, "E111.trimOffspring", {"start": v(6.54, 30.33) * mm, "end": v(5.4, 33.31) * mm});
            skLineSegment(sketch, "E112.trimOffspring", {"start": v(5, 34.38) * mm, "end": v(3.86, 37.36) * mm});
            skLineSegment(sketch, "E113.trimOffspring", {"start": v(1.9, 42.47) * mm, "end": v(0, 47.46) * mm});
            skLineSegment(sketch, "E114.trimOffspring", {"start": v(3.45, 38.43) * mm, "end": v(2.31, 41.4) * mm});
            skLineSegment(sketch, "E115.trimOffspring", {"start": v(-2.31, 41.4) * mm, "end": v(-3.45, 38.43) * mm});
            skLineSegment(sketch, "E116.trimOffspring", {"start": v(-5.4, 33.31) * mm, "end": v(-8.09, 26.29) * mm});
            skLineSegment(sketch, "E117.trimOffspring", {"start": v(-8.5, 25.22) * mm, "end": v(-9.06, 23.73) * mm});
            skLineSegment(sketch, "E118.trimOffspring", {"start": v(-10.04, 21.17) * mm, "end": v(-11.18, 18.2) * mm});
            skLineSegment(sketch, "E119.trimOffspring", {"start": v(-11.59, 17.12) * mm, "end": v(-12.72, 14.14) * mm});
            skLineSegment(sketch, "E120.trimOffspring", {"start": v(-13.13, 13.08) * mm, "end": v(-14.27, 10.1) * mm});
            skLineSegment(sketch, "E121.trimOffspring", {"start": v(-14.68, 9.03) * mm, "end": v(-15.82, 6.05) * mm});
            skLineSegment(sketch, "E122.trimOffspring", {"start": v(-16.22, 4.98) * mm, "end": v(-18.13, 0) * mm});
            skLineSegment(sketch, "E123", {"start": v(-9.63, 22.24) * mm, "end": v(-9.06, 23.73) * mm});
            skLineSegment(sketch, "E124.trimOffspring", {"start": v(-15.82, -6.05) * mm, "end": v(-14.68, -9.03) * mm});
            skLineSegment(sketch, "E125.trimOffspring", {"start": v(-14.27, -10.1) * mm, "end": v(-13.13, -13.08) * mm});
            skLineSegment(sketch, "E126.trimOffspring", {"start": v(-12.72, -14.14) * mm, "end": v(-11.59, -17.12) * mm});
            skLineSegment(sketch, "E127.trimOffspring", {"start": v(-11.18, -18.2) * mm, "end": v(-10.04, -21.17) * mm});
            skLineSegment(sketch, "E128.trimOffspring", {"start": v(-9.63, -22.24) * mm, "end": v(-8.5, -25.22) * mm});
            skLineSegment(sketch, "E129.trimOffspring", {"start": v(-6.54, -30.33) * mm, "end": v(-5.4, -33.31) * mm});
            skLineSegment(sketch, "E130.trimOffspring", {"start": v(-5, -34.38) * mm, "end": v(-3.86, -37.36) * mm});
            skLineSegment(sketch, "E131.trimOffspring", {"start": v(-3.45, -38.43) * mm, "end": v(-2.31, -41.4) * mm});
            skLineSegment(sketch, "E132.trimOffspring", {"start": v(-1.9, -42.47) * mm, "end": v(0, -47.46) * mm});
            skLineSegment(sketch, "E133", {"start": v(-6.95, -29.26) * mm, "end": v(-8.09, -26.29) * mm});
            skLineSegment(sketch, "E134", {"start": v(-5, 34.38) * mm, "end": v(-3.86, 37.36) * mm});
            skLineSegment(sketch, "E135.0", {"start": v(18.13, 16.02) * mm, "end": v(6.12, 47.46) * mm});
            skLineSegment(sketch, "E136.MirrorCS", {"start": v(-18.13, 26.7) * mm, "end": v(-10.2, 47.46) * mm});
            skLineSegment(sketch, "E137.MirrorCS", {"start": v(-18.13, 16.02) * mm, "end": v(-6.12, 47.46) * mm});
            skLineSegment(sketch, "E138.MirrorCS", {"start": v(18.13, -16.02) * mm, "end": v(6.12, -47.46) * mm});
            skLineSegment(sketch, "E139.MirrorCS", {"start": v(-18.13, -16.02) * mm, "end": v(-6.12, -47.46) * mm});
            skSolve(sketch);
        }
        {
            var Q0;
            Q0=makeQuery(id+"F0.imprint","IMPRINT",FACE,{"disambiguationData":[TD([[makeQuery(id+"F0.imprint","IMPRINT",EDGE,{"derivedFrom":sQuery(id+"F0.wireOp",EDGE,"E9.0")}),1.0]])]});
            var Q1;
            Q1=makeQuery(id+"F0.imprint","IMPRINT",FACE,{"disambiguationData":[TD([[makeQuery(id+"F0.imprint","IMPRINT",EDGE,{"derivedFrom":sQuery(id+"F0.wireOp",EDGE,"E8.0")}),1.0]])]});
            var Q2;
            Q2=makeQuery(id+"F0.imprint","IMPRINT",FACE,{"disambiguationData":[TD([[makeQuery(id+"F0.imprint","IMPRINT",EDGE,{"derivedFrom":sQuery(id+"F0.wireOp",EDGE,"E20")}),-1.0]])]});
            var Q3;
            Q3=makeQuery(id+"F0.imprint","IMPRINT",FACE,{"disambiguationData":[TD([[makeQuery(id+"F0.imprint","IMPRINT",EDGE,{"derivedFrom":sQuery(id+"F0.wireOp",EDGE,"E12")}),1.0]])]});
            var Q4;
            Q4=makeQuery(id+"F0.imprint","IMPRINT",FACE,{"disambiguationData":[TD([[makeQuery(id+"F0.imprint","IMPRINT",EDGE,{"derivedFrom":sQuery(id+"F0.wireOp",EDGE,"E37")}),1.0]])]});
            var Q5;
            {var subQ1=sQuery(id+"F0.wireOp",EDGE,"E3");Q5=makeQuery(id+"F0.imprint","IMPRINT",FACE,{"disambiguationData":[TD([[makeQuery(id+"F0.imprint","IMPRINT",EDGE,{"derivedFrom":subQ1}),-1.0]])]});}
            var Q6;
            {var subQ1=sQuery(id+"F0.wireOp",EDGE,"E5.3");Q6=makeQuery(id+"F0.imprint","IMPRINT",FACE,{"disambiguationData":[TD([[makeQuery(id+"F0.imprint","IMPRINT",EDGE,{"derivedFrom":subQ1}),1.0]])]});}
            var Q7;
            {var subQ0=sQuery(id+"F0.wireOp",EDGE,"E2");Q7=makeQuery(id+"F0.imprint","IMPRINT",FACE,{"disambiguationData":[TD([[makeQuery(id+"F0.imprint","IMPRINT",EDGE,{"derivedFrom":subQ0}),-1.0]])]});}
            var Q8;
            {var subQ4=sQuery(id+"F0.wireOp",EDGE,"E40");Q8=makeQuery(id+"F0.imprint","IMPRINT",FACE,{"disambiguationData":[TD([[makeQuery(id+"F0.imprint","IMPRINT",EDGE,{"derivedFrom":subQ4}),1.0]])]});}
            var Q9;
            {var subQ1=sQuery(id+"F0.wireOp",EDGE,"E1");Q9=makeQuery(id+"F0.imprint","IMPRINT",FACE,{"disambiguationData":[TD([[makeQuery(id+"F0.imprint","IMPRINT",EDGE,{"derivedFrom":subQ1}),-1.0]])]});}
            var Q10;
            {var subQ1=sQuery(id+"F0.wireOp",EDGE,"E5.1");Q10=makeQuery(id+"F0.imprint","IMPRINT",FACE,{"disambiguationData":[TD([[makeQuery(id+"F0.imprint","IMPRINT",EDGE,{"derivedFrom":subQ1}),1.0]])]});}
            var Q11;
            {var subQ0=sQuery(id+"F0.wireOp",EDGE,"E4");Q11=makeQuery(id+"F0.imprint","IMPRINT",FACE,{"disambiguationData":[TD([[makeQuery(id+"F0.imprint","IMPRINT",EDGE,{"derivedFrom":subQ0}),-1.0]])]});}
            var Q12;
            {var subQ4=sQuery(id+"F0.wireOp",EDGE,"E56");Q12=makeQuery(id+"F0.imprint","IMPRINT",FACE,{"disambiguationData":[TD([[makeQuery(id+"F0.imprint","IMPRINT",EDGE,{"derivedFrom":subQ4}),1.0]])]});}
            var Q13;
            {var subQ3=sQuery(id+"F0.wireOp",EDGE,"E6.0");Q13=makeQuery(id+"F0.imprint","IMPRINT",FACE,{"disambiguationData":[TD([[makeQuery(id+"F0.imprint","IMPRINT",EDGE,{"derivedFrom":subQ3}),-1.0]])]});}
            var Q14;
            {var subQ3=sQuery(id+"F0.wireOp",EDGE,"E61.0");Q14=makeQuery(id+"F0.imprint","IMPRINT",FACE,{"disambiguationData":[TD([[makeQuery(id+"F0.imprint","IMPRINT",EDGE,{"derivedFrom":subQ3}),-1.0]])]});}
            var Q15;
            {var subQ3=sQuery(id+"F0.wireOp",EDGE,"E62.0");Q15=makeQuery(id+"F0.imprint","IMPRINT",FACE,{"disambiguationData":[TD([[makeQuery(id+"F0.imprint","IMPRINT",EDGE,{"derivedFrom":subQ3}),-1.0]])]});}
            var Q16;
            {var subQ3=sQuery(id+"F0.wireOp",EDGE,"E7.0");Q16=makeQuery(id+"F0.imprint","IMPRINT",FACE,{"disambiguationData":[TD([[makeQuery(id+"F0.imprint","IMPRINT",EDGE,{"derivedFrom":subQ3}),-1.0]])]});}
            var Q17;
            {var subQ0=sQuery(id+"F0.wireOp",EDGE,"E5.1");Q17=makeQuery(id+"F0.imprint","IMPRINT",FACE,{"disambiguationData":[TD([[makeQuery(id+"F0.imprint","IMPRINT",EDGE,{"derivedFrom":subQ0}),-1.0]])]});}
            var Q18;
            {var subQ0=sQuery(id+"F0.wireOp",EDGE,"E5.0");Q18=makeQuery(id+"F0.imprint","IMPRINT",FACE,{"disambiguationData":[TD([[makeQuery(id+"F0.imprint","IMPRINT",EDGE,{"derivedFrom":subQ0}),-1.0]])]});}
            var Q19;
            {var subQ0=sQuery(id+"F0.wireOp",EDGE,"E5.3");Q19=makeQuery(id+"F0.imprint","IMPRINT",FACE,{"disambiguationData":[TD([[makeQuery(id+"F0.imprint","IMPRINT",EDGE,{"derivedFrom":subQ0}),-1.0]])]});}
            var Q20;
            {var subQ0=sQuery(id+"F0.wireOp",EDGE,"E5.2");Q20=makeQuery(id+"F0.imprint","IMPRINT",FACE,{"disambiguationData":[TD([[makeQuery(id+"F0.imprint","IMPRINT",EDGE,{"derivedFrom":subQ0}),-1.0]])]});}
            var Q21;
            {var subQ3=sQuery(id+"F0.wireOp",EDGE,"E136.MirrorCS");Q21=makeQuery(id+"F0.imprint","IMPRINT",FACE,{"disambiguationData":[TD([[makeQuery(id+"F0.imprint","IMPRINT",EDGE,{"derivedFrom":subQ3}),1.0]])]});}
            extrude(context, id + "F1", {"entities" : qUnion([Q0, Q1, Q2, Q3, Q4, Q5, Q6, Q7, Q8, Q9, Q10, Q11, Q12, Q13, Q14, Q15, Q16, Q17, Q18, Q19, Q20, Q21]), "depth" : 2.54 * mm, "offsetDistance" : 25.4 * mm});
        }
        {
            var Q0;
            Q0=makeQuery(id+"F1.opExtrude","CAP_FACE",FACE,{"disambiguationData":[OSD([sQuery(id+"F0.wireOp",EDGE,"E0.bottom"),sQuery(id+"F0.wireOp",EDGE,"E0.left"),sQuery(id+"F0.wireOp",EDGE,"E6.0")])],"isStart":false});
            var sketch = newSketch(context, id + "F2", { "sketchPlane" : qUnion([Q0])});
            skLineSegment(sketch, "E140.bottom", {"start": v(-18.13, 47.46) * mm, "end": v(18.6, 47.46) * mm});
            skLineSegment(sketch, "E140.top", {"start": v(-18.13, -47.52) * mm, "end": v(18.6, -47.52) * mm});
            skLineSegment(sketch, "E140.left", {"start": v(-18.13, 47.46) * mm, "end": v(-18.13, -47.52) * mm});
            skLineSegment(sketch, "E140.right", {"start": v(18.6, 47.46) * mm, "end": v(18.6, -47.52) * mm});
            skSolve(sketch);
        }
        {
            var Q0;
            Q0 = qSketchRegion(id + "F2", true);
            extrude(context, id + "F3", {"entities" : qUnion([Q0]), "depth" : 2.54 * mm, "offsetDistance" : 25.4 * mm});
        }
    });
